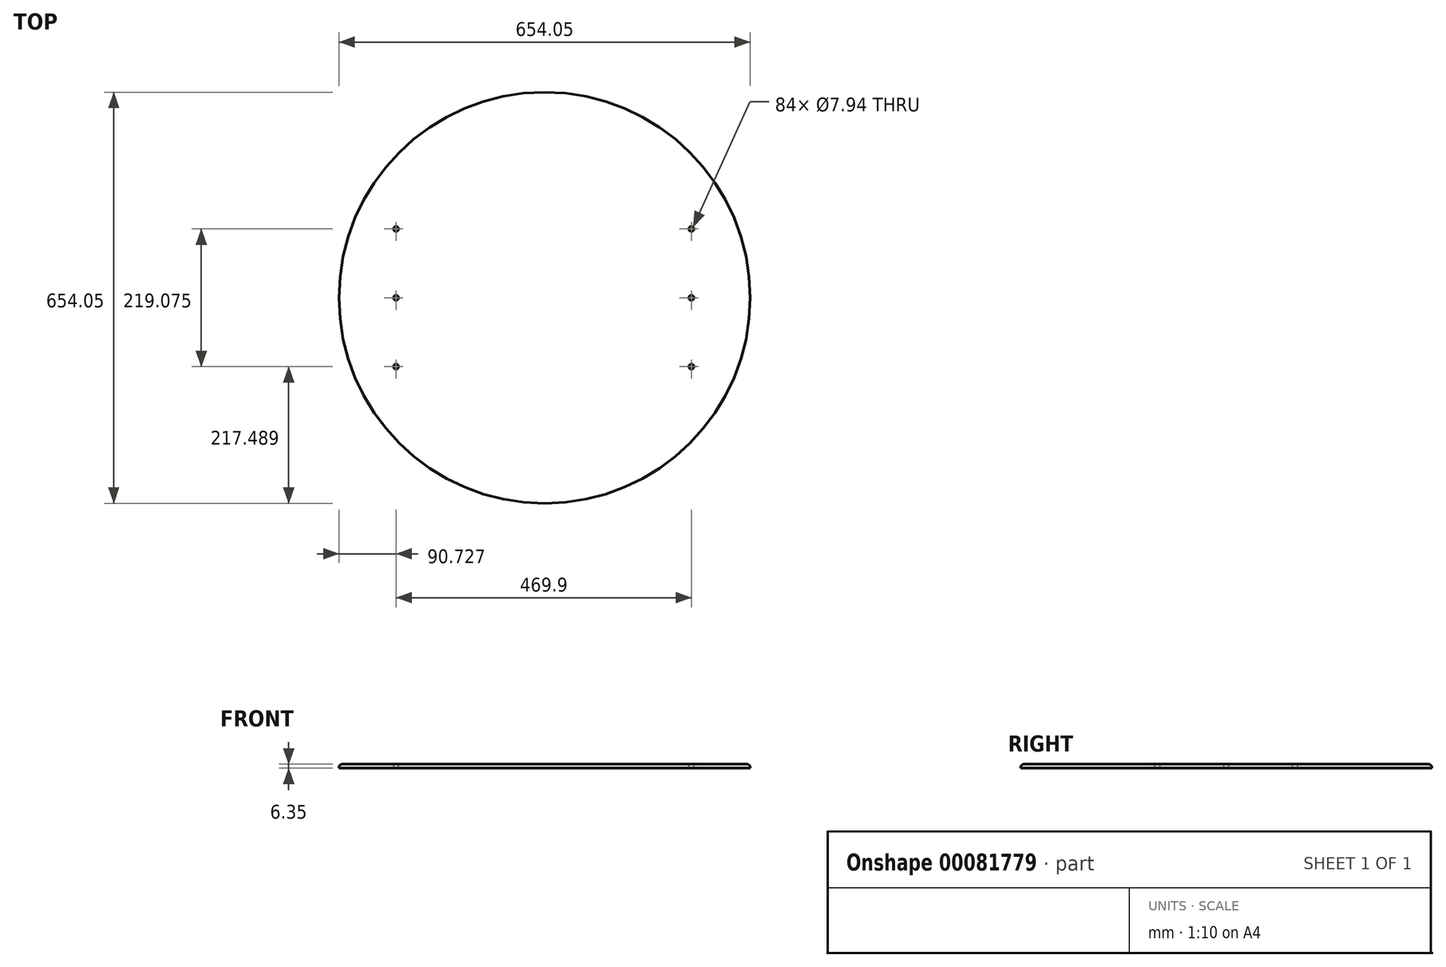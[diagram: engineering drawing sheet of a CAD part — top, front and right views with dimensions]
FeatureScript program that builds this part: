
annotation { "Feature Type Name" : "Feature", "Feature Type Description" : "" }
export const myFeature = defineFeature(function(context is Context, id is Id, definition is map)
    precondition{}
    {
        {
            var Q0;
            Q0=qCreatedBy(makeId("Top.planeOp"),FACE);
            var sketch = newSketch(context, id + "F0", { "sketchPlane" : qUnion([Q0])});
            skCircle(sketch, "E0", {"center": v(-23.67, 22.68) * mm, "radius": 327.03 * mm});
            skSolve(sketch);
        }
        {
            var Q0;
            Q0=makeQuery(id+"F0.imprint","IMPRINT",FACE,{"disambiguationData":[TD([[makeQuery(id+"F0.imprint","IMPRINT",EDGE,{"derivedFrom":sQuery(id+"F0.wireOp",EDGE,"E0")}),1.0]])]});
            extrude(context, id + "F1", {"entities" : qUnion([Q0]), "oppositeDirection" : true, "depth" : 6.35 * mm});
        }
        {
            var Q0;
            Q0=makeQuery(id+"F1.opExtrude","CAP_FACE",FACE,{"disambiguationData":[OSD([sQuery(id+"F0.wireOp",EDGE,"E0")])],"isStart":true});
            var sketch = newSketch(context, id + "F2", { "sketchPlane" : qUnion([Q0])});
            skPoint(sketch, "E1.orphan", {"position": v(-25.02, 349.7) * mm});
            skPoint(sketch, "E2.end.orphan", {"position": v(-25.02, -304.35) * mm});
            skPoint(sketch, "E2.start.orphan", {"position": v(-25.02, 22.68) * mm});
            skPoint(sketch, "E3", {"position": v(-259.97, 22.68) * mm});
            skPoint(sketch, "E4", {"position": v(209.93, 22.68) * mm});
            skPoint(sketch, "E5.end.orphan", {"position": v(-259.97, -95.45) * mm});
            skPoint(sketch, "E6.start.orphan", {"position": v(-259.97, -51.38) * mm});
            skPoint(sketch, "E7", {"position": v(-259.97, -86.89) * mm});
            skPoint(sketch, "E8", {"position": v(209.93, 132.21) * mm});
            skPoint(sketch, "E9", {"position": v(209.93, -89.64) * mm});
            skPoint(sketch, "E10", {"position": v(209.93, -86.85) * mm});
            skPoint(sketch, "E11", {"position": v(-259.97, 132.21) * mm});
            skSolve(sketch);
        }
        {
            var Q0;
            Q0=sQuery(id+"F2.wireOp",VERTEX,"E3");
            var Q1;
            Q1=sQuery(id+"F2.wireOp",VERTEX,"E4");
            var Q2;
            Q2=makeQuery(id+"F1.opExtrude","SWEPT_BODY",BODY,{"disambiguationData":[OSD([sQuery(id+"F0.wireOp",EDGE,"E0")])]});
            hole(context, id + "F3", {"style" : HoleStyle.SIMPLE, "endStyle" : HoleEndStyle.THROUGH, "holeDiameter" : 7.94 * mm, "locations" : qUnion([Q0, Q1]), "scope" : qUnion([Q2]), "isTappedThrough" : true});
        }
        {
            var Q0;
            Q0=makeQuery(id+"F1.opExtrude","CAP_FACE",FACE,{"disambiguationData":[OSD([sQuery(id+"F0.wireOp",EDGE,"E0")])],"isStart":true});
            var sketch = newSketch(context, id + "F4", { "sketchPlane" : qUnion([Q0])});
            skPoint(sketch, "E12", {"position": v(-259.97, 132.21) * mm});
            skPoint(sketch, "E13", {"position": v(-259.97, -86.86) * mm});
            skPoint(sketch, "E14", {"position": v(209.93, -86.86) * mm});
            skPoint(sketch, "E15", {"position": v(209.93, 132.21) * mm});
            skPoint(sketch, "E16.start.orphan", {"position": v(-259.97, 22.68) * mm});
            skPoint(sketch, "E17.start.orphan", {"position": v(209.93, 22.68) * mm});
            skSolve(sketch);
        }
        {
            var Q0;
            Q0=sQuery(id+"F4.wireOp",VERTEX,"E12");
            var Q1;
            Q1=sQuery(id+"F4.wireOp",VERTEX,"E13");
            var Q2;
            Q2=sQuery(id+"F4.wireOp",VERTEX,"E14");
            var Q3;
            Q3=sQuery(id+"F4.wireOp",VERTEX,"E15");
            var Q4;
            Q4=makeQuery(id+"F1.opExtrude","SWEPT_BODY",BODY,{"disambiguationData":[OSD([sQuery(id+"F0.wireOp",EDGE,"E0")])]});
            hole(context, id + "F5", {"style" : HoleStyle.SIMPLE, "endStyle" : HoleEndStyle.THROUGH, "holeDiameter" : 7.94 * mm, "locations" : qUnion([Q0, Q1, Q2, Q3]), "scope" : qUnion([Q4]), "isTappedThrough" : true});
        }
        {
            var Q0;
            Q0=makeQuery(id+"F1.opExtrude","CAP_EDGE",EDGE,{"disambiguationData":[OSD([sQuery(id+"F0.wireOp",EDGE,"E0")])],"isStart":true});
            fillet(context, id + "F6", {"entities" : qUnion([Q0]), "radius" : 5.08 * mm, "tangentPropagation" : true, "allowEdgeOverflow" : false});
        }
    });
